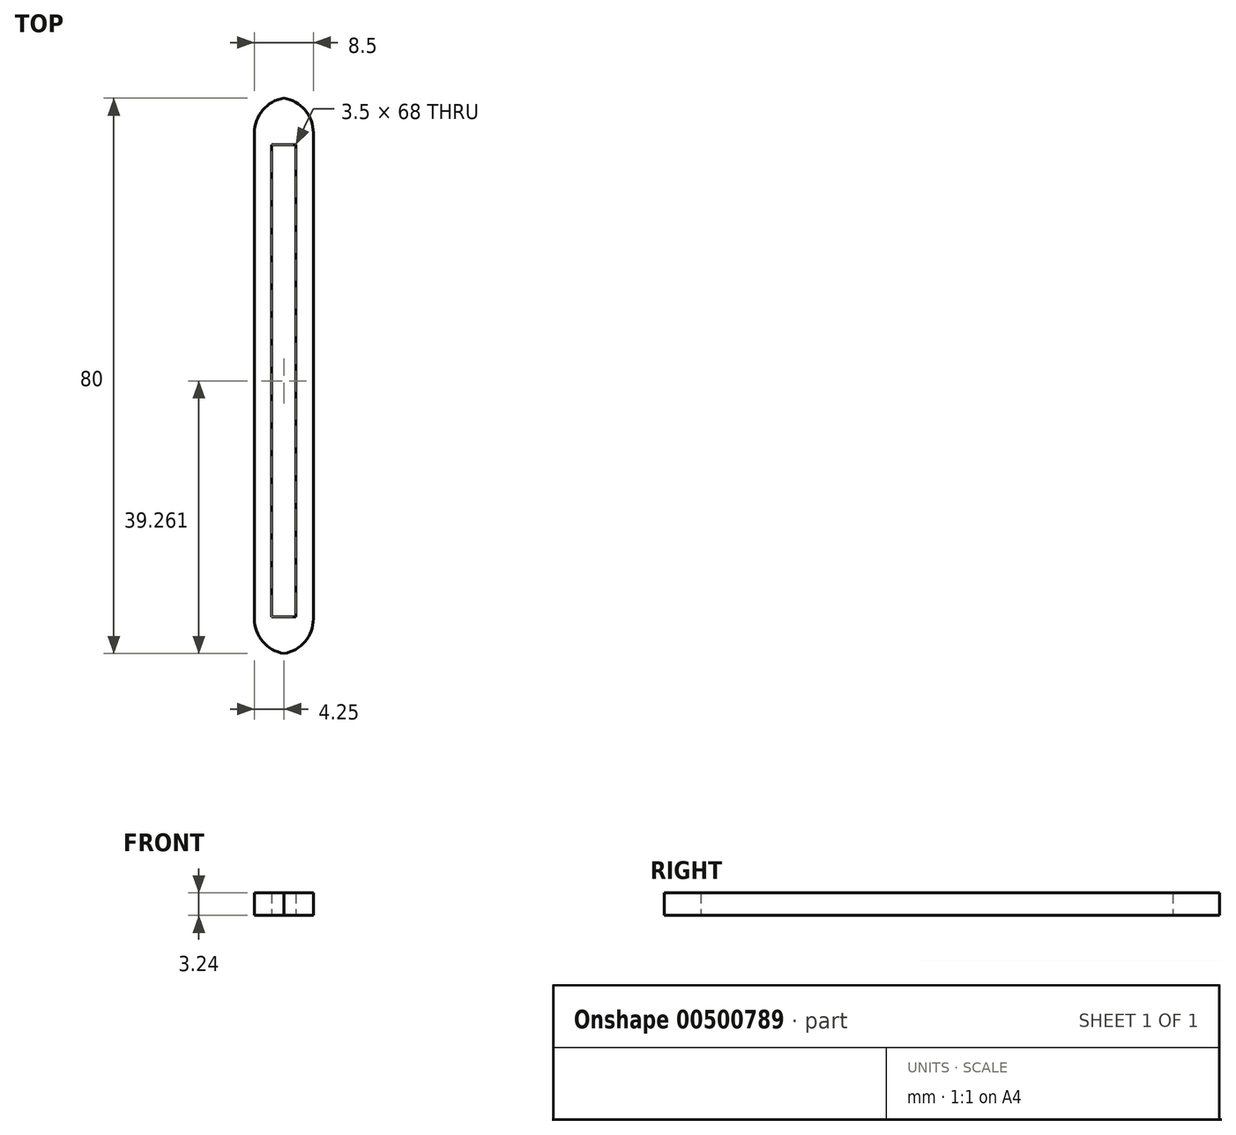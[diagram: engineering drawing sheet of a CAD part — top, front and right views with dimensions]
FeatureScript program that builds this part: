
annotation { "Feature Type Name" : "Feature", "Feature Type Description" : "" }
export const myFeature = defineFeature(function(context is Context, id is Id, definition is map)
    precondition{}
    {
        {
            var Q0;
            Q0=qCreatedBy(makeId("Top.planeOp"),FACE);
            var sketch = newSketch(context, id + "F0", { "sketchPlane" : qUnion([Q0])});
            skLineSegment(sketch, "E0.bottom", {"start": v(4.25, 35) * mm, "end": v(-4.25, 35) * mm});
            skLineSegment(sketch, "E0.top", {"start": v(4.25, -35) * mm, "end": v(-4.25, -35) * mm});
            skLineSegment(sketch, "E0.left", {"start": v(4.25, 35) * mm, "end": v(4.25, -35) * mm});
            skLineSegment(sketch, "E0.right", {"start": v(-4.25, 35) * mm, "end": v(-4.25, -35) * mm});
            skPoint(sketch, "E0.middle", {"position": v(0, 0) * mm});
            skArc(sketch, "E1", {"start": v(-4.25, 35) * mm, "mid": v(-3.04, 38.28) * mm, "end": v(0, 40) * mm});
            skArc(sketch, "E2", {"start": v(4.25, 35) * mm, "mid": v(3.04, 38.28) * mm, "end": v(0, 40) * mm});
            skArc(sketch, "E3", {"start": v(-4.25, -35) * mm, "mid": v(-3.04, -38.28) * mm, "end": v(0, -40) * mm});
            skArc(sketch, "E4", {"start": v(0, -40) * mm, "mid": v(3.04, -38.28) * mm, "end": v(4.25, -35) * mm});
            skLineSegment(sketch, "E5.bottom", {"start": v(-1.75, 33.26) * mm, "end": v(1.75, 33.26) * mm});
            skLineSegment(sketch, "E5.top", {"start": v(-1.75, -34.74) * mm, "end": v(1.75, -34.74) * mm});
            skLineSegment(sketch, "E5.left", {"start": v(-1.75, 33.26) * mm, "end": v(-1.75, -34.74) * mm});
            skLineSegment(sketch, "E5.right", {"start": v(1.75, 33.26) * mm, "end": v(1.75, -34.74) * mm});
            skPoint(sketch, "E5.middle", {"position": v(0, -0.74) * mm});
            skLineSegment(sketch, "E6", {"start": v(0, 0) * mm, "end": v(0, 33.26) * mm});
            skLineSegment(sketch, "E7", {"start": v(0, -35) * mm, "end": v(0, 0) * mm});
            skSolve(sketch);
        }
        {
            var Q0;
            Q0=makeQuery(id+"F0.imprint","IMPRINT",FACE,{"disambiguationData":[TD([[makeQuery(id+"F0.imprint","IMPRINT",EDGE,{"derivedFrom":sQuery(id+"F0.wireOp",EDGE,"E0.bottom")}),1.0]])]});
            var Q1;
            Q1=makeQuery(id+"F0.imprint","IMPRINT",FACE,{"disambiguationData":[TD([[makeQuery(id+"F0.imprint","IMPRINT",EDGE,{"derivedFrom":sQuery(id+"F0.wireOp",EDGE,"E0.bottom")}),-1.0]])]});
            var Q2;
            Q2=makeQuery(id+"F0.imprint","IMPRINT",FACE,{"disambiguationData":[TD([[makeQuery(id+"F0.imprint","IMPRINT",EDGE,{"derivedFrom":sQuery(id+"F0.wireOp",EDGE,"E0.top")}),1.0]])]});
            extrude(context, id + "F1", {"entities" : qUnion([Q0, Q1, Q2]), "depth" : 3.24 * mm, "offsetDistance" : 25 * mm});
        }
    });
